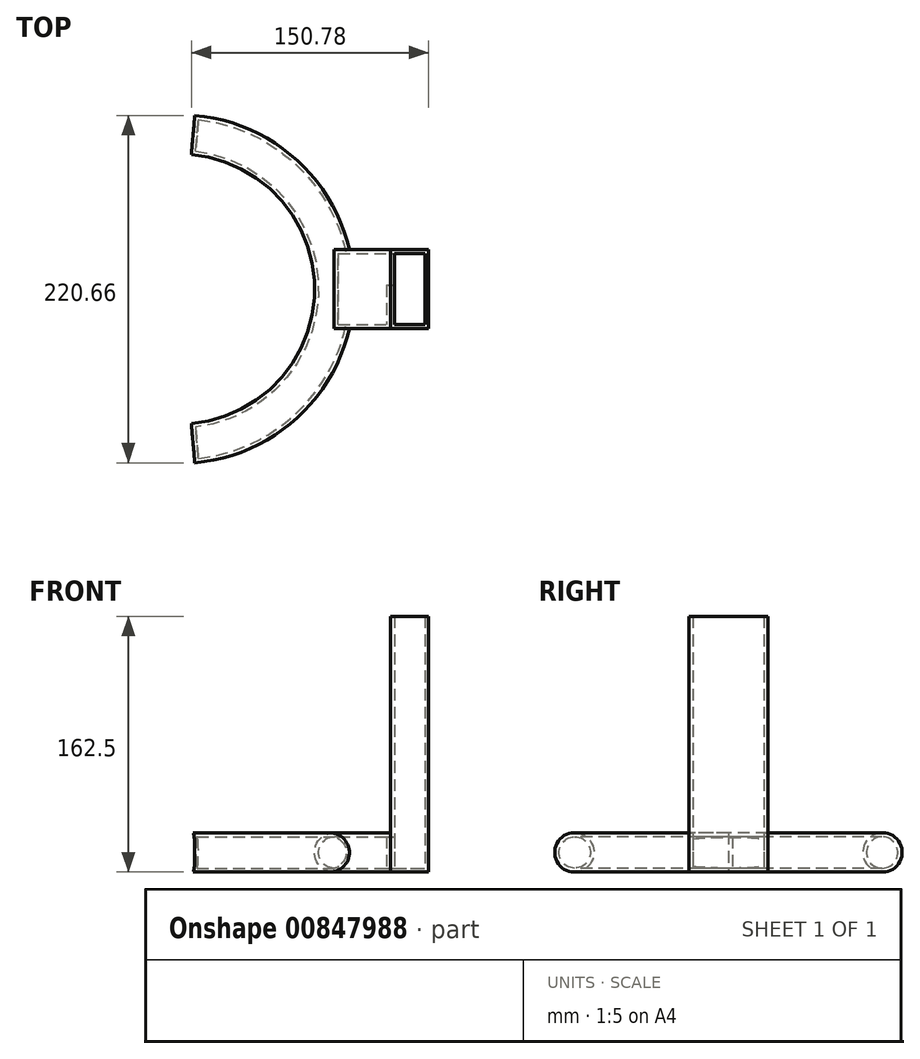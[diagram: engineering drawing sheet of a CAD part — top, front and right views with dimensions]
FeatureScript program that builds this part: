
annotation { "Feature Type Name" : "Feature", "Feature Type Description" : "" }
export const myFeature = defineFeature(function(context is Context, id is Id, definition is map)
    precondition{}
    {
        {
            var Q0;
            Q0=qCreatedBy(makeId("Front.planeOp"),FACE);
            var sketch = newSketch(context, id + "F0", { "sketchPlane" : qUnion([Q0])});
            skCircle(sketch, "E0", {"center": v(0, 0) * mm, "radius": 12.5 * mm});
            skLineSegment(sketch, "E1", {"start": v(-98.25, 39.77) * mm, "end": v(-98.25, -35.37) * mm});
            skSolve(sketch);
        }
        {
            var Q0;
            Q0=makeQuery(id+"F0.imprint","IMPRINT",FACE,{"disambiguationData":[TD([[makeQuery(id+"F0.imprint","IMPRINT",EDGE,{"derivedFrom":sQuery(id+"F0.wireOp",EDGE,"E0")}),1.0]])]});
            var Q1;
            Q1=sQuery(id+"F0.wireOp",EDGE,"E1");
            revolve(context, id + "F1", {"surfaceOperationType" : NewSurfaceOperationType.NEW, "entities" : qUnion([Q0]), "axis" : qUnion([Q1]), "revolveType" : RevolveType.SYMMETRIC, "angle" : 170 * degree});
        }
        {
            var Q0;
            Q0=qCreatedBy(makeId("Top.planeOp"),FACE);
            var sketch = newSketch(context, id + "F2", { "sketchPlane" : qUnion([Q0])});
            skLineSegment(sketch, "E2.bottom", {"start": v(0, 0) * mm, "end": v(35.66, 0) * mm});
            skLineSegment(sketch, "E2.top", {"start": v(0, -25) * mm, "end": v(35.66, -25) * mm});
            skLineSegment(sketch, "E2.left", {"start": v(0, 0) * mm, "end": v(0, -25) * mm});
            skLineSegment(sketch, "E2.right", {"start": v(35.66, 0) * mm, "end": v(35.66, -25) * mm});
            skLineSegment(sketch, "E3.bottom", {"start": v(0, 0) * mm, "end": v(35.81, 0) * mm});
            skLineSegment(sketch, "E3.top", {"start": v(0, 25) * mm, "end": v(35.81, 25) * mm});
            skLineSegment(sketch, "E3.left", {"start": v(0, 0) * mm, "end": v(0, 25) * mm});
            skLineSegment(sketch, "E3.right", {"start": v(35.81, 0) * mm, "end": v(35.81, 25) * mm});
            skLineSegment(sketch, "E4.bottom", {"start": v(35.81, 25) * mm, "end": v(60, 25) * mm});
            skLineSegment(sketch, "E4.top", {"start": v(35.81, -25) * mm, "end": v(60, -25) * mm});
            skLineSegment(sketch, "E4.left", {"start": v(35.81, 25) * mm, "end": v(35.81, -25) * mm});
            skLineSegment(sketch, "E4.right", {"start": v(60, 25) * mm, "end": v(60, -25) * mm});
            skSolve(sketch);
        }
        {
            var Q0;
            Q0 = qSketchRegion(id + "F2", true);
            extrude(context, id + "F3", {"entities" : qUnion([Q0]), "operationType" : NewBodyOperationType.ADD, "endBound" : BoundingType.SYMMETRIC, "depth" : 25 * mm, "offsetDistance" : 25 * mm});
        }
        {
            var Q0;
            {var subQ3=sQuery(id+"F2.wireOp",EDGE,"E4.bottom");Q0=makeQuery(id+"F2.imprint","IMPRINT",FACE,{"disambiguationData":[TD([[makeQuery(id+"F2.imprint","IMPRINT",EDGE,{"derivedFrom":subQ3}),-1.0]])]});}
            extrude(context, id + "F4", {"entities" : qUnion([Q0]), "operationType" : NewBodyOperationType.ADD, "depth" : 150 * mm, "offsetDistance" : 25 * mm});
        }
        {
            var Q0;
            Q0=makeQuery(id+"F4.opExtrude","CAP_FACE",FACE,{"disambiguationData":[OSD([sQuery(id+"F2.wireOp",EDGE,"E4.bottom"),sQuery(id+"F2.wireOp",EDGE,"E4.top"),sQuery(id+"F2.wireOp",EDGE,"E4.left"),sQuery(id+"F2.wireOp",EDGE,"E4.right")])],"isStart":false});
            shell(context, id + "F5", {"entities" : qUnion([Q0]), "thickness" : 2.5 * mm});
        }
    });
